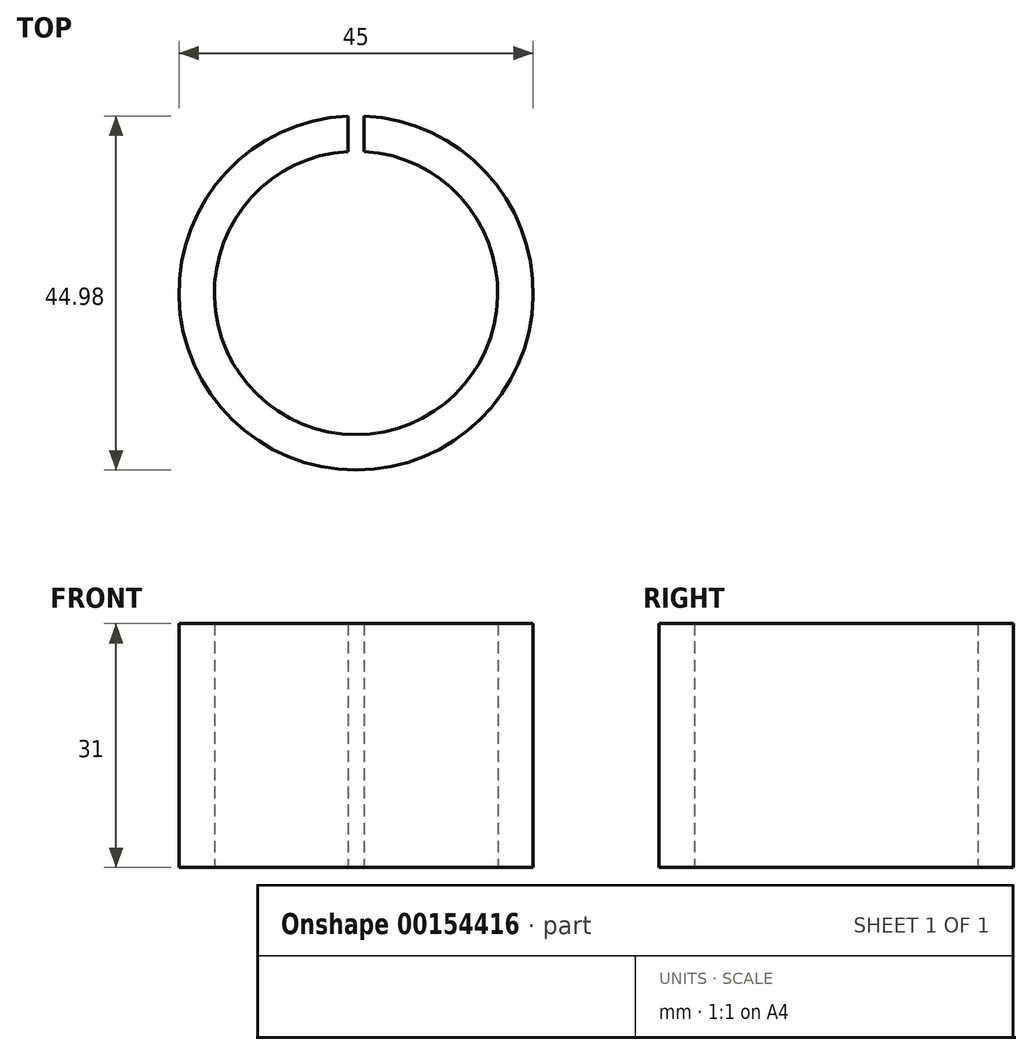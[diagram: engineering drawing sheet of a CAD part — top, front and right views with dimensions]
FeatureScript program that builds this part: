
annotation { "Feature Type Name" : "Feature", "Feature Type Description" : "" }
export const myFeature = defineFeature(function(context is Context, id is Id, definition is map)
    precondition{}
    {
        {
            var Q0;
            Q0=qCreatedBy(makeId("Top.planeOp"),FACE);
            var sketch = newSketch(context, id + "F0", { "sketchPlane" : qUnion([Q0])});
            skCircle(sketch, "E0", {"center": v(0, 0) * mm, "radius": 22.5 * mm});
            skCircle(sketch, "E1", {"center": v(0, 0) * mm, "radius": 18 * mm});
            skSolve(sketch);
        }
        {
            var Q0;
            Q0 = qSketchRegion(id + "F0", true);
            extrude(context, id + "F1", {"entities" : qUnion([Q0]), "depth" : 31 * mm});
        }
        {
            var Q0;
            Q0=makeQuery(id+"F1.opExtrude","CAP_FACE",FACE,{"disambiguationData":[OSD([sQuery(id+"F0.wireOp",EDGE,"E0"),sQuery(id+"F0.wireOp",EDGE,"E1")])],"isStart":false});
            var sketch = newSketch(context, id + "F2", { "sketchPlane" : qUnion([Q0])});
            skLineSegment(sketch, "E2.bottom", {"start": v(1.02, 25.34) * mm, "end": v(-1.02, 25.34) * mm});
            skLineSegment(sketch, "E2.top", {"start": v(1.02, 14.92) * mm, "end": v(-1.02, 14.92) * mm});
            skLineSegment(sketch, "E2.left", {"start": v(1.02, 25.34) * mm, "end": v(1.02, 14.92) * mm});
            skLineSegment(sketch, "E2.right", {"start": v(-1.02, 25.34) * mm, "end": v(-1.02, 14.92) * mm});
            skPoint(sketch, "E2.middle", {"position": v(0, 20.13) * mm});
            skSolve(sketch);
        }
        {
            var Q0;
            Q0 = qSketchRegion(id + "F2", true);
            extrude(context, id + "F3", {"entities" : qUnion([Q0]), "operationType" : NewBodyOperationType.REMOVE, "oppositeDirection" : true, "depth" : 35 * mm});
        }
    });
